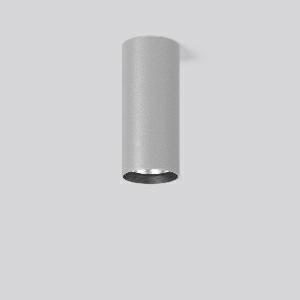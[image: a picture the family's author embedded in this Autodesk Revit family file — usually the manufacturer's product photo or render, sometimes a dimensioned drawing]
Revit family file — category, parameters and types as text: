
# Revit family: heledon_mini_a_931202_004_1_781a
name_source: partatom
category: Lighting Fixtures
units: mm (PartAtom-declared; Revit-internal decimal feet)

## family parameters
Cut with Voids When Loaded = No
Host = Face
Light Source = No
Part Type = Normal
Room Calculation Point = No
Round Connector Dimension = Use Diameter
Shared = No

## types (1)
- HELEDON mini A (1 x LED Modul 940, 2750 lm, 4000)
    Apparent Load = 20 VA
    Approval mark = CE
    CIE Flux Codes = 95 99 100 100 100
    Color Rendering = 92
    Color Temperature = 4000
    Default Elevation = 1800 mm
    Description = Series: HELEDON mini
Cylindrical surface-mounted downlight. Housing: die-cast aluminium, powder-coated. Internal ceiling frame polycarbonate with bayonet mounting. Black plastic ring and recessed LED to prevent glare from the side. Optical assembly with reflector made of MIRO-Silver with 98% total light reflection for outstanding efficiency - can be changed without tools. Best colour rendering index Ra>90. Suitable for Ceiling mounting. Easy installation with a separate ceiling frame with bayonet mounting and plug connection. Driver integrated. Connected via plug-in connector. High quality converter without flickering and stroboscopic effect. The following accessories can be mounted without use of tools: interchangeable lenses, decorative glasses, honeycomb louvre, clear and frosted diffusers, white interchangeable plastic ring. 
Colour: silver
Diameter: 87 mm
Height: 197 mm
Lamp: LED
Socket: without socket
Colour temperature: 4000K
Colour rendering index (CRI): 92
System power: 20 W
Rated luminous flux: 2750 lm
Luminous efficiency: 138 lm/W
Control gear: Regulated power supply
Protection class: I
Type of protection: IP 20
    Height = 197 mm
    Lamp = 1 x LED Modul 940
    Lamp Light Flux = 2750 lm
    Lamp count = 1
    Length = 87 mm
    Lifetime = 50000 h
    Luminous efficacy = 138 lm/W
    Manufacturer = RZB
    ModVariant = No
    Model = 931202.004.1
    Mounting Place = Ceiling
    Mounting Type = Surface mounted
    Number of Poles = 1
    OnlyDefault = Yes
    Power Factor = 1
    Product Name = HELEDON mini A
    Product group = Surface mounted downlights
    ProductGroupID = 302
    Protection Class = Protection class I
    Protection Degree = IP 20
    RLX_Detail_Level = 1
    RLX_Emergency_Light_Flux = 0 lm
    RLX_Emergency_Type = 0
    RLX_Emergency_Type_DB = No
    RlxData = <blob elided: 109029 chars, md5=1c60b319>
    Socket = socket
    Standby Power = 0 W
    System Light Flux = 2750 lm
    System Power = 20 W
    Type Comments = Product without accessories
    Type Image = 931188.004.jpg
    URL = http://relux.com
    VarID = ---
    Voltage = 230 V
    Voltage Range = 220-240 V
    Weight = 0.00 kg
    Width = 0 mm  [stored 0 ft]

note: [stored X ft] marks values corroborated as IEEE doubles in the binary element streams (Revit-internal decimal feet)

## geometry (parser evidence)
native form markers: Blend x4, Sweep x10
no freeform markers — native parametric forms only
